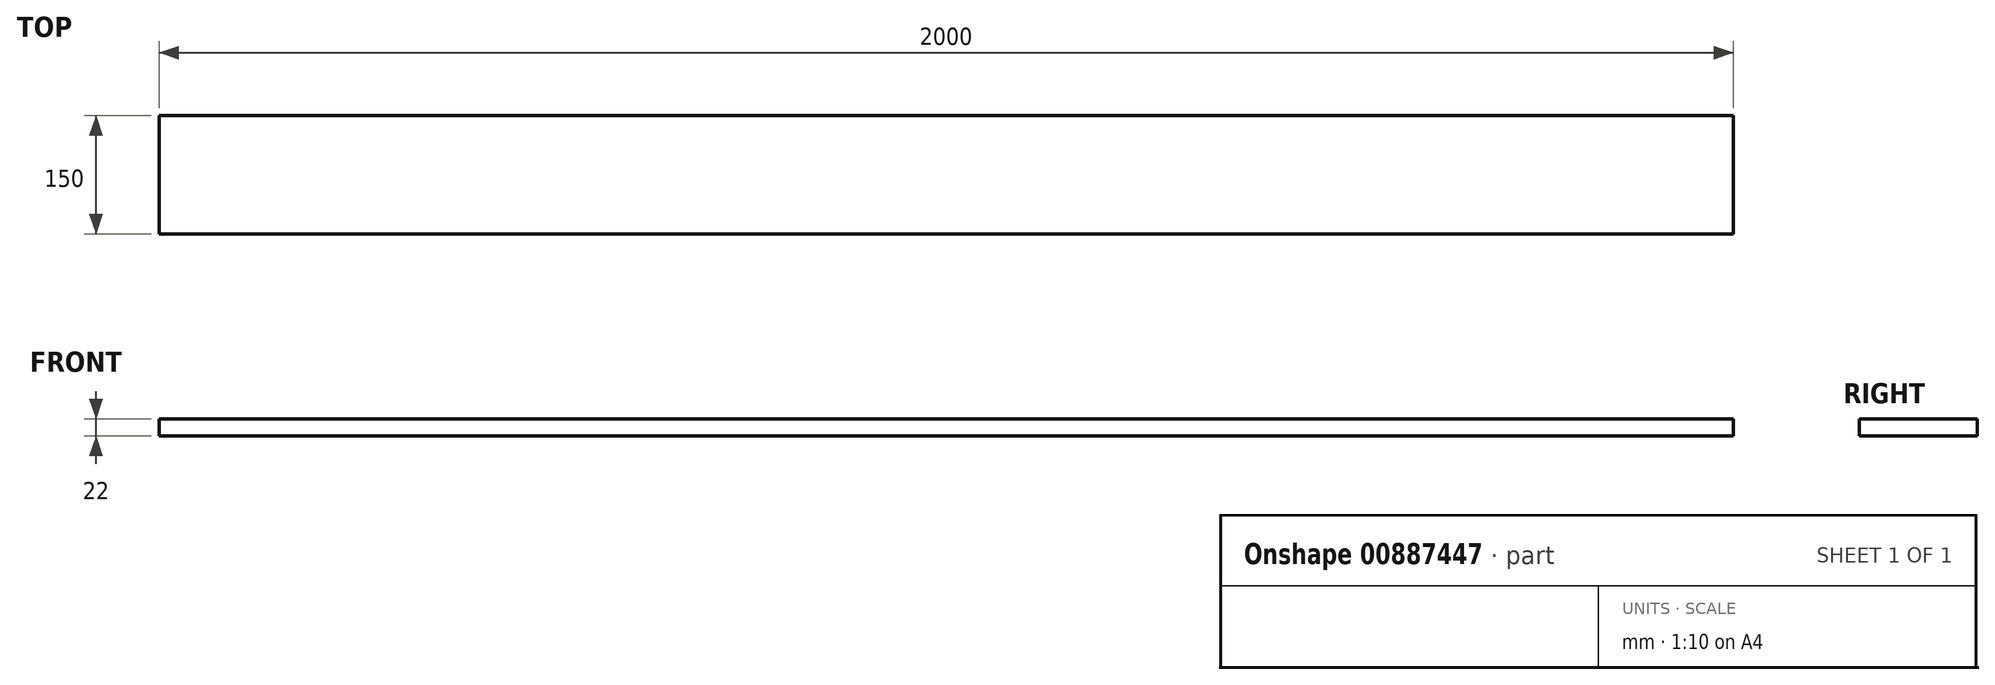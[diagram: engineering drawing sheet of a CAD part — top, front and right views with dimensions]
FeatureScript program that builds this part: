
annotation { "Feature Type Name" : "Feature", "Feature Type Description" : "" }
export const myFeature = defineFeature(function(context is Context, id is Id, definition is map)
    precondition{}
    {
        {
            var Q0;
            Q0=qCreatedBy(makeId("Right.planeOp"),FACE);
            var sketch = newSketch(context, id + "F0", { "sketchPlane" : qUnion([Q0])});
            skLineSegment(sketch, "E0.bottom", {"start": v(75, -1000) * mm, "end": v(-75, -1000) * mm});
            skLineSegment(sketch, "E0.top", {"start": v(75, 1000) * mm, "end": v(-75, 1000) * mm});
            skLineSegment(sketch, "E0.left", {"start": v(75, -1000) * mm, "end": v(75, 1000) * mm});
            skLineSegment(sketch, "E0.right", {"start": v(-75, -1000) * mm, "end": v(-75, 1000) * mm});
            skPoint(sketch, "E0.middle", {"position": v(0, 0) * mm});
            skSolve(sketch);
        }
        {
            var Q0;
            Q0=makeQuery(id+"F0.imprint","IMPRINT",FACE,{"disambiguationData":[TD([[makeQuery(id+"F0.imprint","IMPRINT",EDGE,{"derivedFrom":sQuery(id+"F0.wireOp",EDGE,"E0.bottom")}),-1.0]])]});
            extrude(context, id + "F1", {"entities" : qUnion([Q0]), "depth" : 22 * mm, "offsetDistance" : 25 * mm});
        }
        {
            var Q0;
            Q0=makeQuery(id+"F1.opExtrude","SWEPT_BODY",BODY,{"disambiguationData":[OSD([sQuery(id+"F0.wireOp",EDGE,"E0.bottom"),sQuery(id+"F0.wireOp",EDGE,"E0.top"),sQuery(id+"F0.wireOp",EDGE,"E0.left"),sQuery(id+"F0.wireOp",EDGE,"E0.right")])]});
            var Q1;
            Q1=makeQuery(id+"F1.opExtrude","CAP_EDGE",EDGE,{"disambiguationData":[OSD([sQuery(id+"F0.wireOp",EDGE,"E0.bottom")])],"isStart":true});
            transform(context, id + "F2", {"entities" : qUnion([Q0]), "transformType" : TransformType.ROTATION, "transformAxis" : qUnion([Q1]), "angle" : 90 * degree, "makeCopy" : false});
        }
    });
